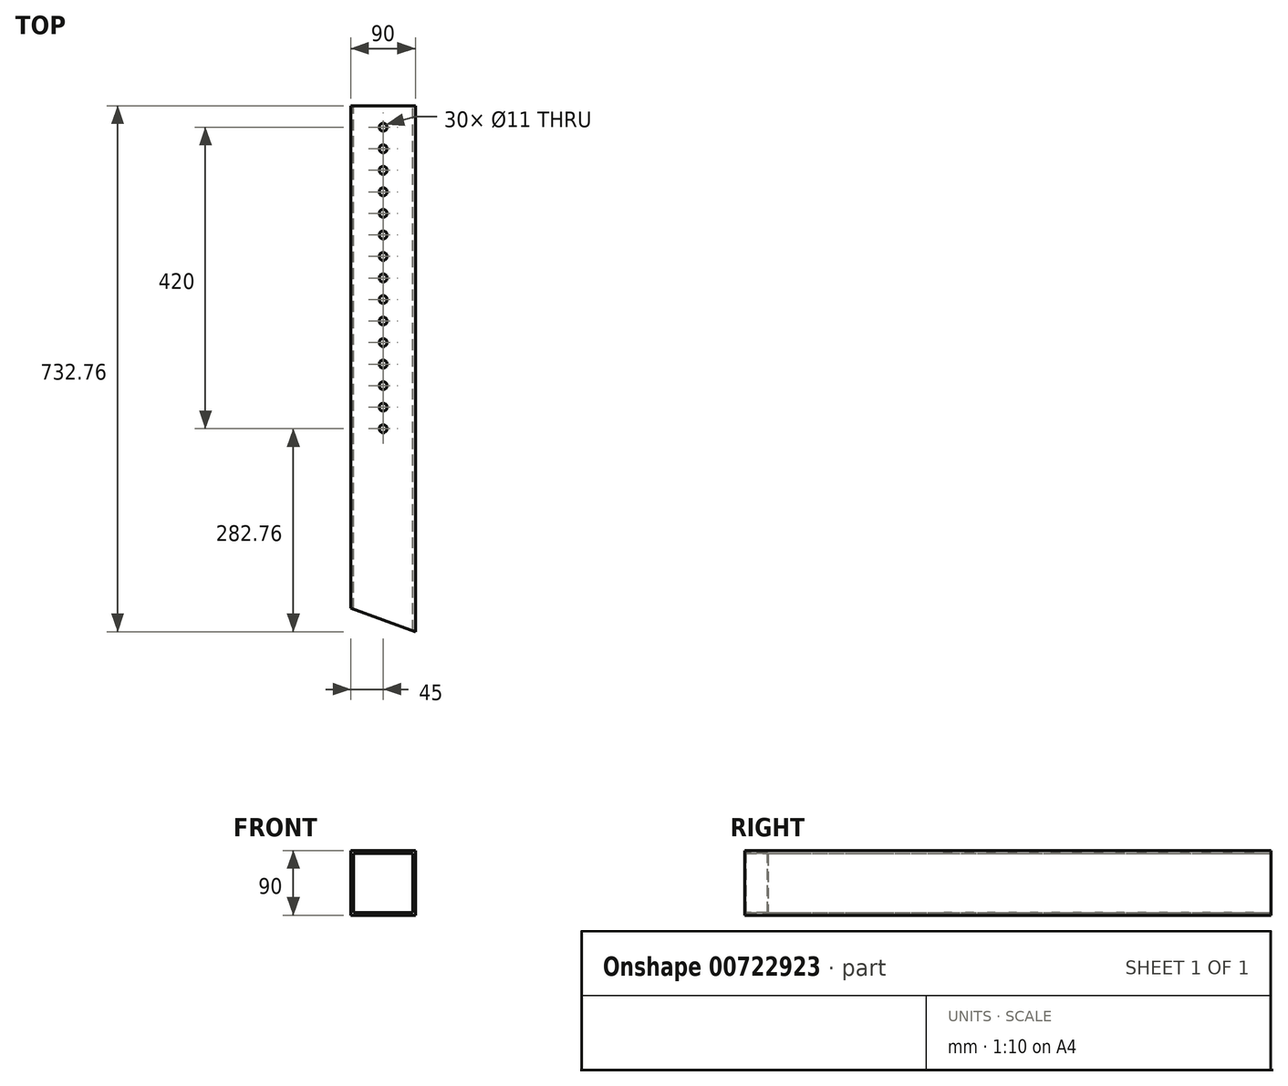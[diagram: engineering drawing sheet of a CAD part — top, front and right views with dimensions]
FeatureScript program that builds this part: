
annotation { "Feature Type Name" : "Feature", "Feature Type Description" : "" }
export const myFeature = defineFeature(function(context is Context, id is Id, definition is map)
    precondition{}
    {
        {
            var Q0;
            Q0=qCreatedBy(makeId("Front.planeOp"),FACE);
            var sketch = newSketch(context, id + "F0", { "sketchPlane" : qUnion([Q0])});
            skLineSegment(sketch, "E0.bottom", {"start": v(0, 0) * mm, "end": v(90, 0) * mm});
            skLineSegment(sketch, "E0.top", {"start": v(0, 90) * mm, "end": v(90, 90) * mm});
            skLineSegment(sketch, "E0.left", {"start": v(0, 0) * mm, "end": v(0, 90) * mm});
            skLineSegment(sketch, "E0.right", {"start": v(90, 0) * mm, "end": v(90, 90) * mm});
            skLineSegment(sketch, "E1.bottom", {"start": v(3.6, 3.6) * mm, "end": v(86.1, 3.6) * mm});
            skLineSegment(sketch, "E1.top", {"start": v(3.6, 86.1) * mm, "end": v(86.1, 86.1) * mm});
            skLineSegment(sketch, "E1.left", {"start": v(3.6, 3.6) * mm, "end": v(3.6, 86.1) * mm});
            skLineSegment(sketch, "E1.right", {"start": v(86.1, 3.6) * mm, "end": v(86.1, 86.1) * mm});
            skSolve(sketch);
        }
        {
            var Q0;
            Q0=makeQuery(id+"F0.imprint","IMPRINT",FACE,{"disambiguationData":[TD([[makeQuery(id+"F0.imprint","IMPRINT",EDGE,{"derivedFrom":sQuery(id+"F0.wireOp",EDGE,"E0.bottom")}),1.0]])]});
            extrude(context, id + "F1", {"entities" : qUnion([Q0]), "depth" : 700 * mm, "offsetDistance" : 25 * mm});
        }
        {
            var Q0;
            Q0=makeQuery(id+"F1.opExtrude","SWEPT_FACE",FACE,{"disambiguationData":[OSD([sQuery(id+"F0.wireOp",EDGE,"E0.top")])]});
            var sketch = newSketch(context, id + "F2", { "sketchPlane" : qUnion([Q0])});
            skLineSegment(sketch, "E2", {"start": v(0, -700) * mm, "end": v(90, -700) * mm});
            skLineSegment(sketch, "E3", {"start": v(90, -700) * mm, "end": v(90, -732.76) * mm});
            skLineSegment(sketch, "E4", {"start": v(90, -732.76) * mm, "end": v(0, -700) * mm});
            skSolve(sketch);
        }
        {
            var Q0;
            Q0 = qSketchRegion(id + "F2", true);
            extrude(context, id + "F3", {"entities" : qUnion([Q0]), "operationType" : NewBodyOperationType.ADD, "oppositeDirection" : true, "depth" : 90 * mm, "offsetDistance" : 25 * mm});
        }
        {
            var Q0;
            Q0=makeQuery(id+"F3.opExtrude","SWEPT_FACE",FACE,{"disambiguationData":[OSD([sQuery(id+"F2.wireOp",EDGE,"E2")])]});
            var sketch = newSketch(context, id + "F4", { "sketchPlane" : qUnion([Q0])});
            skLineSegment(sketch, "E5.bottom", {"start": v(-3.6, 3.6) * mm, "end": v(-86.1, 3.6) * mm});
            skLineSegment(sketch, "E5.top", {"start": v(-3.6, 86.1) * mm, "end": v(-86.1, 86.1) * mm});
            skLineSegment(sketch, "E5.left", {"start": v(-3.6, 3.6) * mm, "end": v(-3.6, 86.1) * mm});
            skLineSegment(sketch, "E5.right", {"start": v(-86.1, 3.6) * mm, "end": v(-86.1, 86.1) * mm});
            skSolve(sketch);
        }
        {
            var Q0;
            Q0 = qSketchRegion(id + "F4", true);
            extrude(context, id + "F5", {"entities" : qUnion([Q0]), "operationType" : NewBodyOperationType.REMOVE, "oppositeDirection" : true, "depth" : 40 * mm, "offsetDistance" : 25 * mm});
        }
        {
            var Q0;
            Q0=makeQuery(id+"F3.boolean.opBoolean","MERGE",FACE,{"derivedFrom":[makeQuery(id+"F1.opExtrude","SWEPT_FACE",FACE,{"disambiguationData":[OSD([sQuery(id+"F0.wireOp",EDGE,"E0.top")])]}),makeQuery(id+"F3.opExtrude","CAP_FACE",FACE,{"disambiguationData":[OSD([sQuery(id+"F2.wireOp",EDGE,"E2"),sQuery(id+"F2.wireOp",EDGE,"E3"),sQuery(id+"F2.wireOp",EDGE,"E4")])],"isStart":true})]});
            var sketch = newSketch(context, id + "F6", { "sketchPlane" : qUnion([Q0])});
            skCircle(sketch, "E6", {"center": v(45, -30) * mm, "radius": 5.5 * mm});
            skCircle(sketch, "E7.0.1.0", {"center": v(45, -60) * mm, "radius": 5.5 * mm});
            skCircle(sketch, "E7.0.2.0", {"center": v(45, -90) * mm, "radius": 5.5 * mm});
            skCircle(sketch, "E7.0.3.0", {"center": v(45, -120) * mm, "radius": 5.5 * mm});
            skCircle(sketch, "E7.0.4.0", {"center": v(45, -150) * mm, "radius": 5.5 * mm});
            skCircle(sketch, "E7.0.5.0", {"center": v(45, -180) * mm, "radius": 5.5 * mm});
            skCircle(sketch, "E7.0.6.0", {"center": v(45, -210) * mm, "radius": 5.5 * mm});
            skCircle(sketch, "E7.0.7.0", {"center": v(45, -240) * mm, "radius": 5.5 * mm});
            skCircle(sketch, "E7.0.8.0", {"center": v(45, -270) * mm, "radius": 5.5 * mm});
            skCircle(sketch, "E7.0.9.0", {"center": v(45, -300) * mm, "radius": 5.5 * mm});
            skCircle(sketch, "E7.0.10.0", {"center": v(45, -330) * mm, "radius": 5.5 * mm});
            skCircle(sketch, "E7.0.11.0", {"center": v(45, -360) * mm, "radius": 5.5 * mm});
            skCircle(sketch, "E7.0.12.0", {"center": v(45, -390) * mm, "radius": 5.5 * mm});
            skCircle(sketch, "E7.0.13.0", {"center": v(45, -420) * mm, "radius": 5.5 * mm});
            skLineSegment(sketch, "E7.direction1", {"start": v(45, -30) * mm, "end": v(70, -30) * mm, "construction": true});
            skLineSegment(sketch, "E7.direction2", {"start": v(45, -30) * mm, "end": v(45, -60) * mm, "construction": true});
            skCircle(sketch, "E8", {"center": v(45, -450) * mm, "radius": 5.5 * mm});
            skSolve(sketch);
        }
        {
            var Q0;
            Q0=makeQuery(id+"F6.imprint","IMPRINT",FACE,{"disambiguationData":[TD([[makeQuery(id+"F6.imprint","IMPRINT",EDGE,{"derivedFrom":sQuery(id+"F6.wireOp",EDGE,"E6")}),1.0]])]});
            var Q1;
            Q1=makeQuery(id+"F6.imprint","IMPRINT",FACE,{"disambiguationData":[TD([[makeQuery(id+"F6.imprint","IMPRINT",EDGE,{"derivedFrom":sQuery(id+"F6.wireOp",EDGE,"E7.0.1.0")}),1.0]])]});
            var Q2;
            Q2=makeQuery(id+"F6.imprint","IMPRINT",FACE,{"disambiguationData":[TD([[makeQuery(id+"F6.imprint","IMPRINT",EDGE,{"derivedFrom":sQuery(id+"F6.wireOp",EDGE,"E7.0.2.0")}),1.0]])]});
            var Q3;
            Q3=makeQuery(id+"F6.imprint","IMPRINT",FACE,{"disambiguationData":[TD([[makeQuery(id+"F6.imprint","IMPRINT",EDGE,{"derivedFrom":sQuery(id+"F6.wireOp",EDGE,"E7.0.3.0")}),1.0]])]});
            var Q4;
            Q4=makeQuery(id+"F6.imprint","IMPRINT",FACE,{"disambiguationData":[TD([[makeQuery(id+"F6.imprint","IMPRINT",EDGE,{"derivedFrom":sQuery(id+"F6.wireOp",EDGE,"E7.0.4.0")}),1.0]])]});
            var Q5;
            Q5=makeQuery(id+"F6.imprint","IMPRINT",FACE,{"disambiguationData":[TD([[makeQuery(id+"F6.imprint","IMPRINT",EDGE,{"derivedFrom":sQuery(id+"F6.wireOp",EDGE,"E7.0.5.0")}),1.0]])]});
            var Q6;
            Q6=makeQuery(id+"F6.imprint","IMPRINT",FACE,{"disambiguationData":[TD([[makeQuery(id+"F6.imprint","IMPRINT",EDGE,{"derivedFrom":sQuery(id+"F6.wireOp",EDGE,"E7.0.6.0")}),1.0]])]});
            var Q7;
            Q7=makeQuery(id+"F6.imprint","IMPRINT",FACE,{"disambiguationData":[TD([[makeQuery(id+"F6.imprint","IMPRINT",EDGE,{"derivedFrom":sQuery(id+"F6.wireOp",EDGE,"E7.0.7.0")}),1.0]])]});
            var Q8;
            Q8=makeQuery(id+"F6.imprint","IMPRINT",FACE,{"disambiguationData":[TD([[makeQuery(id+"F6.imprint","IMPRINT",EDGE,{"derivedFrom":sQuery(id+"F6.wireOp",EDGE,"E7.0.8.0")}),1.0]])]});
            var Q9;
            Q9=makeQuery(id+"F6.imprint","IMPRINT",FACE,{"disambiguationData":[TD([[makeQuery(id+"F6.imprint","IMPRINT",EDGE,{"derivedFrom":sQuery(id+"F6.wireOp",EDGE,"E7.0.9.0")}),1.0]])]});
            var Q10;
            Q10=makeQuery(id+"F6.imprint","IMPRINT",FACE,{"disambiguationData":[TD([[makeQuery(id+"F6.imprint","IMPRINT",EDGE,{"derivedFrom":sQuery(id+"F6.wireOp",EDGE,"E7.0.10.0")}),1.0]])]});
            var Q11;
            Q11=makeQuery(id+"F6.imprint","IMPRINT",FACE,{"disambiguationData":[TD([[makeQuery(id+"F6.imprint","IMPRINT",EDGE,{"derivedFrom":sQuery(id+"F6.wireOp",EDGE,"E7.0.11.0")}),1.0]])]});
            var Q12;
            Q12=makeQuery(id+"F6.imprint","IMPRINT",FACE,{"disambiguationData":[TD([[makeQuery(id+"F6.imprint","IMPRINT",EDGE,{"derivedFrom":sQuery(id+"F6.wireOp",EDGE,"E7.0.12.0")}),1.0]])]});
            var Q13;
            Q13=makeQuery(id+"F6.imprint","IMPRINT",FACE,{"disambiguationData":[TD([[makeQuery(id+"F6.imprint","IMPRINT",EDGE,{"derivedFrom":sQuery(id+"F6.wireOp",EDGE,"E7.0.13.0")}),1.0]])]});
            var Q14;
            Q14=makeQuery(id+"F6.imprint","IMPRINT",FACE,{"disambiguationData":[TD([[makeQuery(id+"F6.imprint","IMPRINT",EDGE,{"derivedFrom":sQuery(id+"F6.wireOp",EDGE,"E8")}),1.0]])]});
            extrude(context, id + "F7", {"entities" : qUnion([Q0, Q1, Q2, Q3, Q4, Q5, Q6, Q7, Q8, Q9, Q10, Q11, Q12, Q13, Q14]), "operationType" : NewBodyOperationType.REMOVE, "endBound" : BoundingType.THROUGH_ALL, "oppositeDirection" : true, "depth" : 25 * mm, "offsetDistance" : 25 * mm});
        }
    });
